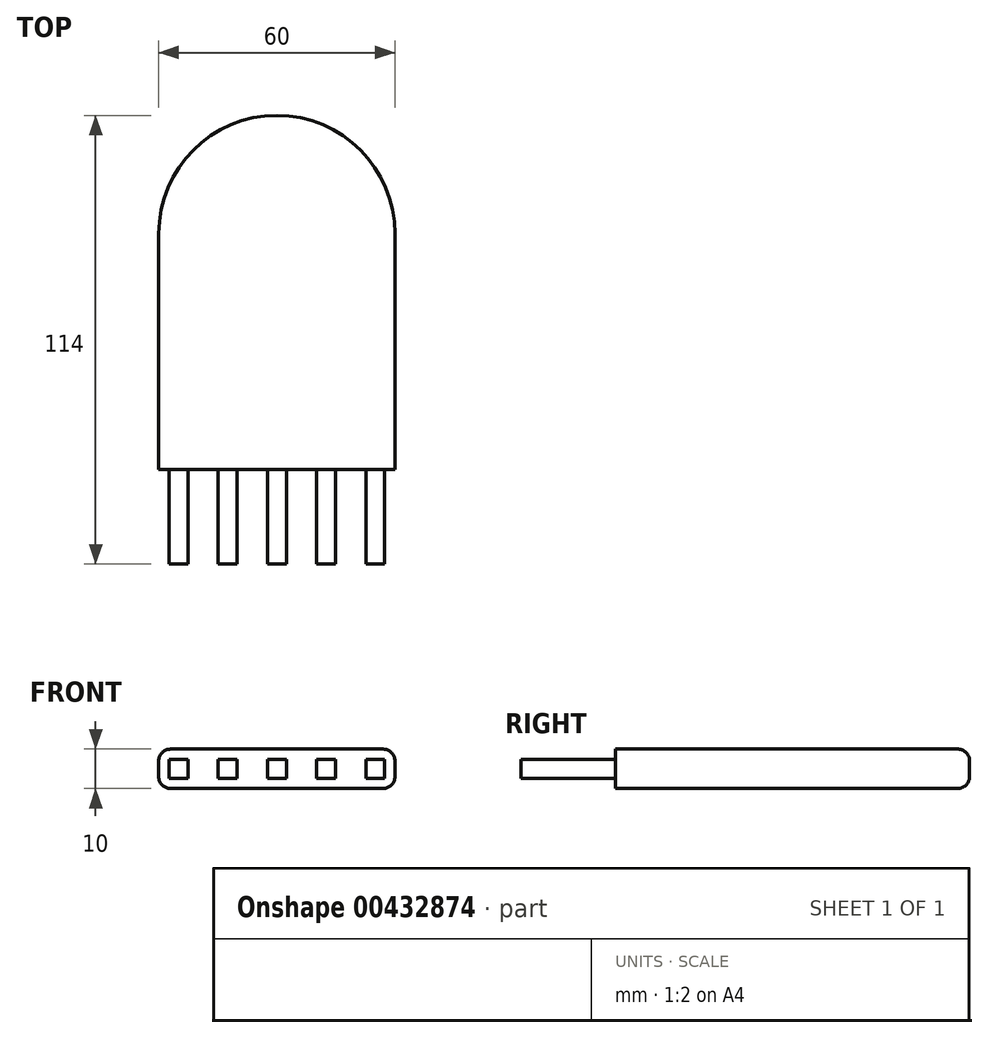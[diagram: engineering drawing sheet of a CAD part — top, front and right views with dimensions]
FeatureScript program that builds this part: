
annotation { "Feature Type Name" : "Feature", "Feature Type Description" : "" }
export const myFeature = defineFeature(function(context is Context, id is Id, definition is map)
    precondition{}
    {
        {
            var Q0;
            Q0=qCreatedBy(makeId("Top.planeOp"),FACE);
            var sketch = newSketch(context, id + "F0", { "sketchPlane" : qUnion([Q0])});
            skLineSegment(sketch, "E0.bottom", {"start": v(30, 0) * mm, "end": v(-30, 0) * mm});
            skLineSegment(sketch, "E0.left", {"start": v(30, 0) * mm, "end": v(30, 60) * mm});
            skLineSegment(sketch, "E0.right", {"start": v(-30, 0) * mm, "end": v(-30, 60) * mm});
            skPoint(sketch, "E0.middle", {"position": v(0, 30) * mm});
            skArc(sketch, "E1", {"start": v(30, 60) * mm, "mid": v(0, 90) * mm, "end": v(-30, 60) * mm});
            skSolve(sketch);
        }
        {
            var Q0;
            Q0 = qSketchRegion(id + "F0", true);
            extrude(context, id + "F1", {"entities" : qUnion([Q0]), "depth" : 10 * mm});
        }
        {
            var Q0;
            Q0=makeQuery(id+"F1.opExtrude","SWEPT_FACE",FACE,{"disambiguationData":[OSD([sQuery(id+"F0.wireOp",EDGE,"E0.bottom")])]});
            var sketch = newSketch(context, id + "F2", { "sketchPlane" : qUnion([Q0])});
            skLineSegment(sketch, "E2.bottom", {"start": v(-22.6, 7.4) * mm, "end": v(-27.4, 7.4) * mm});
            skLineSegment(sketch, "E2.top", {"start": v(-22.6, 2.6) * mm, "end": v(-27.4, 2.6) * mm});
            skLineSegment(sketch, "E2.left", {"start": v(-22.6, 7.4) * mm, "end": v(-22.6, 2.6) * mm});
            skLineSegment(sketch, "E2.right", {"start": v(-27.4, 7.4) * mm, "end": v(-27.4, 2.6) * mm});
            skPoint(sketch, "E2.middle", {"position": v(-25, 5) * mm});
            skLineSegment(sketch, "E3", {"start": v(-25, 10) * mm, "end": v(-25, 0) * mm, "construction": true});
            skLineSegment(sketch, "E4.1.0.0", {"start": v(-10.1, 7.4) * mm, "end": v(-14.9, 7.4) * mm});
            skLineSegment(sketch, "E4.1.0.1", {"start": v(-14.9, 7.4) * mm, "end": v(-14.9, 2.6) * mm});
            skLineSegment(sketch, "E4.1.0.2", {"start": v(-10.1, 2.6) * mm, "end": v(-14.9, 2.6) * mm});
            skLineSegment(sketch, "E4.1.0.3", {"start": v(-10.1, 7.4) * mm, "end": v(-10.1, 2.6) * mm});
            skLineSegment(sketch, "E4.2.0.0", {"start": v(2.4, 7.4) * mm, "end": v(-2.4, 7.4) * mm});
            skLineSegment(sketch, "E4.2.0.1", {"start": v(-2.4, 7.4) * mm, "end": v(-2.4, 2.6) * mm});
            skLineSegment(sketch, "E4.2.0.2", {"start": v(2.4, 2.6) * mm, "end": v(-2.4, 2.6) * mm});
            skLineSegment(sketch, "E4.2.0.3", {"start": v(2.4, 7.4) * mm, "end": v(2.4, 2.6) * mm});
            skLineSegment(sketch, "E4.3.0.0", {"start": v(14.9, 7.4) * mm, "end": v(10.1, 7.4) * mm});
            skLineSegment(sketch, "E4.3.0.1", {"start": v(10.1, 7.4) * mm, "end": v(10.1, 2.6) * mm});
            skLineSegment(sketch, "E4.3.0.2", {"start": v(14.9, 2.6) * mm, "end": v(10.1, 2.6) * mm});
            skLineSegment(sketch, "E4.3.0.3", {"start": v(14.9, 7.4) * mm, "end": v(14.9, 2.6) * mm});
            skLineSegment(sketch, "E4.4.0.0", {"start": v(27.4, 7.4) * mm, "end": v(22.6, 7.4) * mm});
            skLineSegment(sketch, "E4.4.0.1", {"start": v(22.6, 7.4) * mm, "end": v(22.6, 2.6) * mm});
            skLineSegment(sketch, "E4.4.0.2", {"start": v(27.4, 2.6) * mm, "end": v(22.6, 2.6) * mm});
            skLineSegment(sketch, "E4.4.0.3", {"start": v(27.4, 7.4) * mm, "end": v(27.4, 2.6) * mm});
            skLineSegment(sketch, "E4.direction1", {"start": v(-27.4, 7.4) * mm, "end": v(-14.9, 7.4) * mm, "construction": true});
            skSolve(sketch);
        }
        {
            var Q0;
            Q0 = qSketchRegion(id + "F2", true);
            extrude(context, id + "F3", {"entities" : qUnion([Q0]), "operationType" : NewBodyOperationType.ADD, "depth" : 24 * mm});
        }
        {
            var Q0;
            Q0=makeQuery(id+"F1.opExtrude","CAP_EDGE",EDGE,{"disambiguationData":[OSD([sQuery(id+"F0.wireOp",EDGE,"E0.left")])],"isStart":false});
            var Q1;
            Q1=makeQuery(id+"F1.opExtrude","CAP_EDGE",EDGE,{"disambiguationData":[OSD([sQuery(id+"F0.wireOp",EDGE,"E0.left")])],"isStart":true});
            fillet(context, id + "F4", {"entities" : qUnion([Q0, Q1]), "radius" : 3 * mm, "tangentPropagation" : true, "allowEdgeOverflow" : false});
        }
    });
